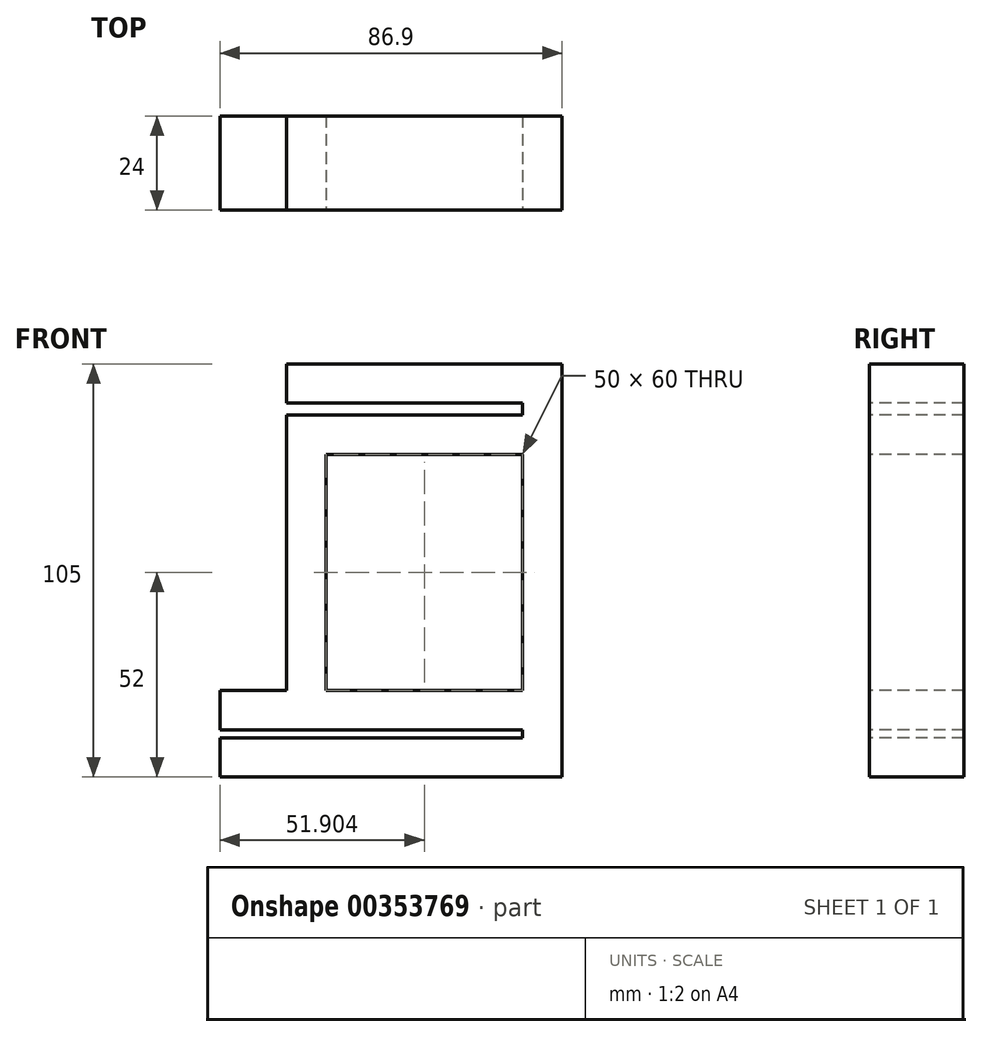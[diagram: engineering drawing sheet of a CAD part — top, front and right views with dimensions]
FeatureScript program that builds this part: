
annotation { "Feature Type Name" : "Feature", "Feature Type Description" : "" }
export const myFeature = defineFeature(function(context is Context, id is Id, definition is map)
    precondition{}
    {
        {
            var Q0;
            Q0=qCreatedBy(makeId("Top.planeOp"),FACE);
            var sketch = newSketch(context, id + "F0", { "sketchPlane" : qUnion([Q0])});
            skLineSegment(sketch, "E0.bottom", {"start": v(-43.45, 12) * mm, "end": v(43.45, 12) * mm});
            skLineSegment(sketch, "E0.top", {"start": v(-43.45, -12) * mm, "end": v(43.45, -12) * mm});
            skLineSegment(sketch, "E0.left", {"start": v(-43.45, 12) * mm, "end": v(-43.45, -12) * mm});
            skLineSegment(sketch, "E0.right", {"start": v(43.45, 12) * mm, "end": v(43.45, -12) * mm});
            skPoint(sketch, "E0.middle", {"position": v(0, 0) * mm});
            skSolve(sketch);
        }
        {
            var Q0;
            Q0 = qSketchRegion(id + "F0", true);
            extrude(context, id + "F1", {"entities" : qUnion([Q0]), "depth" : 10 * mm});
        }
        {
            var Q0;
            Q0=makeQuery(id+"F1.opExtrude","CAP_FACE",FACE,{"disambiguationData":[OSD([sQuery(id+"F0.wireOp",EDGE,"E0.bottom"),sQuery(id+"F0.wireOp",EDGE,"E0.top"),sQuery(id+"F0.wireOp",EDGE,"E0.left"),sQuery(id+"F0.wireOp",EDGE,"E0.right")])],"isStart":false});
            var sketch = newSketch(context, id + "F2", { "sketchPlane" : qUnion([Q0])});
            skLineSegment(sketch, "E1.bottom", {"start": v(43.45, 12) * mm, "end": v(33.45, 12) * mm});
            skLineSegment(sketch, "E1.top", {"start": v(43.45, -12) * mm, "end": v(33.45, -12) * mm});
            skLineSegment(sketch, "E1.left", {"start": v(43.45, 12) * mm, "end": v(43.45, -12) * mm});
            skLineSegment(sketch, "E1.right", {"start": v(33.45, 12) * mm, "end": v(33.45, -12) * mm});
            skSolve(sketch);
        }
        {
            var Q0;
            Q0 = qSketchRegion(id + "F2", true);
            extrude(context, id + "F3", {"entities" : qUnion([Q0]), "operationType" : NewBodyOperationType.ADD, "depth" : 95 * mm});
        }
        {
            var Q0;
            Q0=makeQuery(id+"F3.opExtrude","SWEPT_FACE",FACE,{"disambiguationData":[OSD([sQuery(id+"F2.wireOp",EDGE,"E1.right")])]});
            var sketch = newSketch(context, id + "F4", { "sketchPlane" : qUnion([Q0])});
            skLineSegment(sketch, "E2.bottom", {"start": v(-12, 12) * mm, "end": v(12, 12) * mm});
            skLineSegment(sketch, "E2.top", {"start": v(-12, 22) * mm, "end": v(12, 22) * mm});
            skLineSegment(sketch, "E2.left", {"start": v(-12, 12) * mm, "end": v(-12, 22) * mm});
            skLineSegment(sketch, "E2.right", {"start": v(12, 12) * mm, "end": v(12, 22) * mm});
            skSolve(sketch);
        }
        {
            var Q0;
            Q0 = qSketchRegion(id + "F4", true);
            var Q1;
            Q1=makeQuery(id+"F1.opExtrude","SWEPT_FACE",FACE,{"disambiguationData":[OSD([sQuery(id+"F0.wireOp",EDGE,"E0.left")])]});
            extrude(context, id + "F5", {"entities" : qUnion([Q0]), "operationType" : NewBodyOperationType.ADD, "endBound" : BoundingType.UP_TO_SURFACE, "endBoundEntityFace" : qUnion([Q1]), "depth" : 25 * mm});
        }
        {
            var Q0;
            Q0=makeQuery(id+"F5.boolean.opBoolean","MERGE",FACE,{"derivedFrom":[makeQuery(id+"F3.boolean.opBoolean","MERGE",FACE,{"derivedFrom":[makeQuery(id+"F1.opExtrude","SWEPT_FACE",FACE,{"disambiguationData":[OSD([sQuery(id+"F0.wireOp",EDGE,"E0.top")])]}),makeQuery(id+"F3.opExtrude","SWEPT_FACE",FACE,{"disambiguationData":[OSD([sQuery(id+"F2.wireOp",EDGE,"E1.top")])]})]}),makeQuery(id+"F5.opExtrude","SWEPT_FACE",FACE,{"disambiguationData":[OSD([sQuery(id+"F4.wireOp",EDGE,"E2.right")])]})]});
            var sketch = newSketch(context, id + "F6", { "sketchPlane" : qUnion([Q0])});
            skLineSegment(sketch, "E3", {"start": v(-26.55, 22) * mm, "end": v(-26.55, 92) * mm});
            skLineSegment(sketch, "E4", {"start": v(-26.55, 92) * mm, "end": v(33.45, 92) * mm});
            skLineSegment(sketch, "E5", {"start": v(33.45, 92) * mm, "end": v(33.45, 82) * mm});
            skLineSegment(sketch, "E6", {"start": v(33.45, 82) * mm, "end": v(-16.55, 82) * mm});
            skLineSegment(sketch, "E7", {"start": v(-16.55, 82) * mm, "end": v(-16.55, 22) * mm});
            skLineSegment(sketch, "E8", {"start": v(33.45, 105) * mm, "end": v(-26.55, 105) * mm});
            skLineSegment(sketch, "E9", {"start": v(-26.55, 105) * mm, "end": v(-26.55, 95) * mm});
            skLineSegment(sketch, "E10", {"start": v(-26.55, 95) * mm, "end": v(33.45, 95) * mm});
            skSolve(sketch);
        }
        {
            var Q0;
            Q0 = qSketchRegion(id + "F6", true);
            var Q1;
            {var subQ0=sQuery(id+"F6.wireOp",EDGE,"E3");Q1=makeQuery(id+"F6.imprint","IMPRINT",FACE,{"disambiguationData":[TD([[makeQuery(id+"F6.imprint","IMPRINT",EDGE,{"derivedFrom":subQ0}),-1.0]])]});}
            var Q2;
            {var subQ0=sQuery(id+"F6.wireOp",EDGE,"E8");Q2=makeQuery(id+"F6.imprint","IMPRINT",FACE,{"disambiguationData":[TD([[makeQuery(id+"F6.imprint","IMPRINT",EDGE,{"derivedFrom":subQ0}),1.0]])]});}
            var Q3;
            Q3=makeQuery(id+"F5.boolean.opBoolean","MERGE",FACE,{"derivedFrom":[makeQuery(id+"F3.boolean.opBoolean","MERGE",FACE,{"derivedFrom":[makeQuery(id+"F1.opExtrude","SWEPT_FACE",FACE,{"disambiguationData":[OSD([sQuery(id+"F0.wireOp",EDGE,"E0.bottom")])]}),makeQuery(id+"F3.opExtrude","SWEPT_FACE",FACE,{"disambiguationData":[OSD([sQuery(id+"F2.wireOp",EDGE,"E1.bottom")])]})]}),makeQuery(id+"F5.opExtrude","SWEPT_FACE",FACE,{"disambiguationData":[OSD([sQuery(id+"F4.wireOp",EDGE,"E2.left")])]})]});
            extrude(context, id + "F7", {"entities" : qUnion([Q0, Q1, Q2]), "operationType" : NewBodyOperationType.ADD, "endBound" : BoundingType.UP_TO_SURFACE, "oppositeDirection" : true, "endBoundEntityFace" : qUnion([Q3]), "depth" : 25 * mm});
        }
    });
